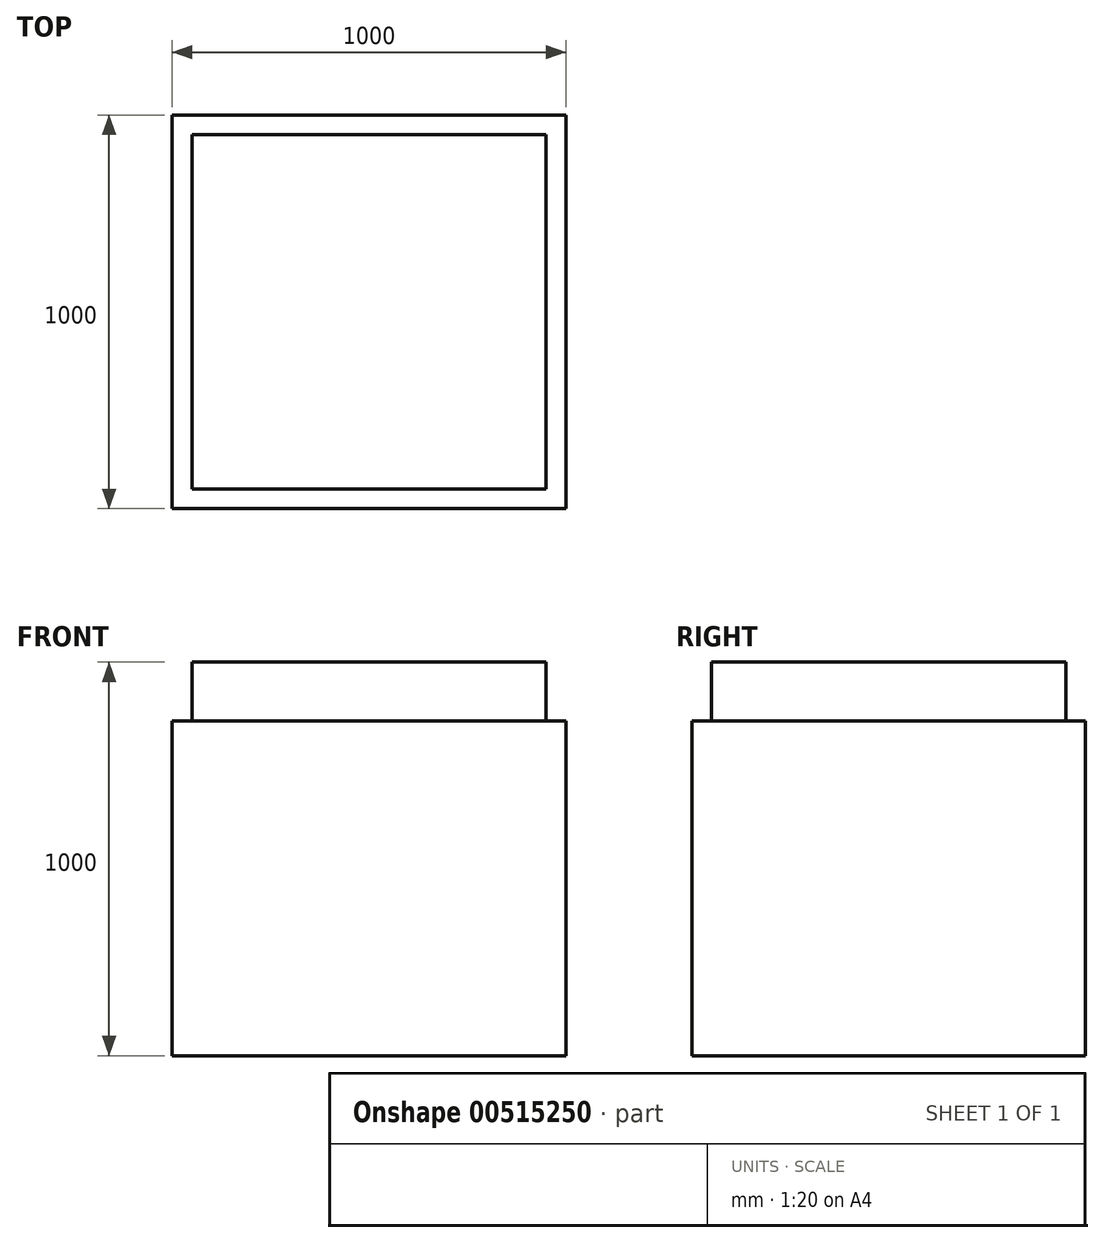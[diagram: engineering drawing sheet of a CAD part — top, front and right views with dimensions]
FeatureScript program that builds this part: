
annotation { "Feature Type Name" : "Feature", "Feature Type Description" : "" }
export const myFeature = defineFeature(function(context is Context, id is Id, definition is map)
    precondition{}
    {
        {
            var Q0;
            Q0=qCreatedBy(makeId("Top.planeOp"),FACE);
            var sketch = newSketch(context, id + "F0", { "sketchPlane" : qUnion([Q0])});
            skLineSegment(sketch, "E0.bottom", {"start": v(500, -500) * mm, "end": v(-500, -500) * mm});
            skLineSegment(sketch, "E0.top", {"start": v(500, 500) * mm, "end": v(-500, 500) * mm});
            skLineSegment(sketch, "E0.left", {"start": v(500, -500) * mm, "end": v(500, 500) * mm});
            skLineSegment(sketch, "E0.right", {"start": v(-500, -500) * mm, "end": v(-500, 500) * mm});
            skPoint(sketch, "E0.middle", {"position": v(0, 0) * mm});
            skSolve(sketch);
        }
        {
            var Q0;
            Q0=makeQuery(id+"F0.imprint","IMPRINT",FACE,{"disambiguationData":[TD([[makeQuery(id+"F0.imprint","IMPRINT",EDGE,{"derivedFrom":sQuery(id+"F0.wireOp",EDGE,"E0.bottom")}),-1.0]])]});
            extrude(context, id + "F1", {"entities" : qUnion([Q0]), "oppositeDirection" : true, "depth" : 1000 * mm, "offsetDistance" : 25 * mm});
        }
        {
            var Q0;
            Q0=makeQuery(id+"F1.opExtrude","CAP_FACE",FACE,{"disambiguationData":[OSD([sQuery(id+"F0.wireOp",EDGE,"E0.bottom"),sQuery(id+"F0.wireOp",EDGE,"E0.top"),sQuery(id+"F0.wireOp",EDGE,"E0.left"),sQuery(id+"F0.wireOp",EDGE,"E0.right")])],"isStart":true});
            var sketch = newSketch(context, id + "F2", { "sketchPlane" : qUnion([Q0])});
            skLineSegment(sketch, "E1.bottom", {"start": v(450, 450) * mm, "end": v(-450, 450) * mm});
            skLineSegment(sketch, "E1.top", {"start": v(450, -450) * mm, "end": v(-450, -450) * mm});
            skLineSegment(sketch, "E1.left", {"start": v(450, 450) * mm, "end": v(450, -450) * mm});
            skLineSegment(sketch, "E1.right", {"start": v(-450, 450) * mm, "end": v(-450, -450) * mm});
            skPoint(sketch, "E1.middle", {"position": v(0, 0) * mm});
            skSolve(sketch);
        }
        {
            var Q0;
            Q0=makeQuery(id+"F2.imprint","IMPRINT",FACE,{"disambiguationData":[TD([[makeQuery(id+"F2.imprint","IMPRINT",EDGE,{"derivedFrom":sQuery(id+"F2.wireOp",EDGE,"E1.bottom")}),-1.0]])]});
            extrude(context, id + "F3", {"entities" : qUnion([Q0]), "operationType" : NewBodyOperationType.REMOVE, "oppositeDirection" : true, "depth" : 150 * mm, "offsetDistance" : 25 * mm});
        }
    });
